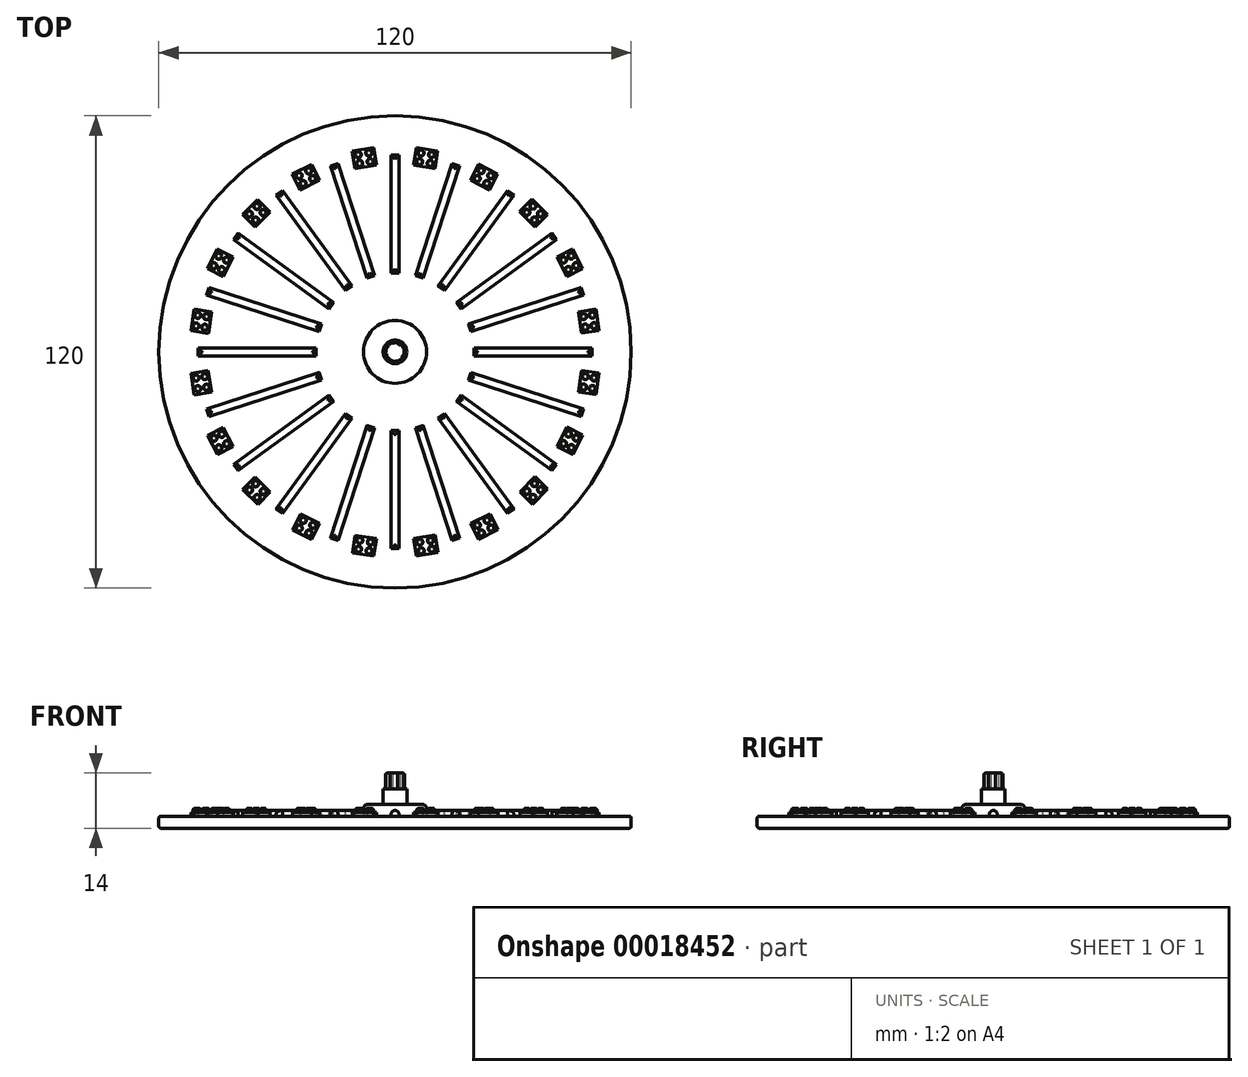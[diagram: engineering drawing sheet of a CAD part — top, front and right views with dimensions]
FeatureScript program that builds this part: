
annotation { "Feature Type Name" : "Feature", "Feature Type Description" : "" }
export const myFeature = defineFeature(function(context is Context, id is Id, definition is map)
    precondition{}
    {
        {
            var Q0;
            Q0=qCreatedBy(makeId("Top.planeOp"),FACE);
            var sketch = newSketch(context, id + "F0", { "sketchPlane" : qUnion([Q0])});
            skCircle(sketch, "E0", {"center": v(0, 0) * mm, "radius": 60 * mm});
            skSolve(sketch);
        }
        {
            var Q0;
            Q0=makeQuery(id+"F0.imprint","IMPRINT",FACE,{"disambiguationData":[TD([[makeQuery(id+"F0.imprint","IMPRINT",EDGE,{"derivedFrom":sQuery(id+"F0.wireOp",EDGE,"E0")}),1.0]])]});
            extrude(context, id + "F1", {"entities" : qUnion([Q0]), "depth" : 3 * mm});
        }
        {
            var Q0;
            Q0=makeQuery(id+"F1.opExtrude","CAP_EDGE",EDGE,{"disambiguationData":[OSD([sQuery(id+"F0.wireOp",EDGE,"E0")])],"isStart":false});
            var Q1;
            Q1=makeQuery(id+"F1.opExtrude","CAP_EDGE",EDGE,{"disambiguationData":[OSD([sQuery(id+"F0.wireOp",EDGE,"E0")])],"isStart":true});
            fillet(context, id + "F2", {"entities" : qUnion([Q0, Q1]), "radius" : 0.5 * mm, "tangentPropagation" : true, "allowEdgeOverflow" : false});
        }
        {
            var Q0;
            Q0=makeQuery(id+"F1.opExtrude","CAP_FACE",FACE,{"disambiguationData":[OSD([sQuery(id+"F0.wireOp",EDGE,"E0")])],"isStart":false});
            var sketch = newSketch(context, id + "F3", { "sketchPlane" : qUnion([Q0])});
            skLineSegment(sketch, "E1", {"start": v(0, 0) * mm, "end": v(0, 59.5) * mm, "construction": true});
            skCircle(sketch, "E2", {"center": v(0, 0) * mm, "radius": 20 * mm, "construction": true});
            skCircle(sketch, "E3", {"center": v(0, 0) * mm, "radius": 50 * mm, "construction": true});
            skCircle(sketch, "E4", {"center": v(0, 0) * mm, "radius": 35 * mm, "construction": true});
            skLineSegment(sketch, "E5.rect.bottom", {"start": v(1, 49.99) * mm, "end": v(-1, 49.99) * mm});
            skLineSegment(sketch, "E5.rect.top", {"start": v(1, 20.01) * mm, "end": v(-1, 20.01) * mm});
            skLineSegment(sketch, "E5.rect.left", {"start": v(1, 49.99) * mm, "end": v(1, 20.01) * mm});
            skLineSegment(sketch, "E5.rect.right", {"start": v(-1, 49.99) * mm, "end": v(-1, 20.01) * mm});
            skPoint(sketch, "E5.rect.middle", {"position": v(0, 35) * mm});
            skCircle(sketch, "E6", {"center": v(0, 0) * mm, "radius": 8 * mm});
            skCircle(sketch, "E7", {"center": v(0, 0) * mm, "radius": 45 * mm, "construction": true});
            skSolve(sketch);
        }
        {
            var Q0;
            Q0=makeQuery(id+"F3.imprint","IMPRINT",FACE,{"disambiguationData":[TD([[makeQuery(id+"F3.imprint","IMPRINT",EDGE,{"derivedFrom":sQuery(id+"F3.wireOp",EDGE,"E5.rect.bottom")}),1.0]])]});
            extrude(context, id + "F4", {"entities" : qUnion([Q0]), "depth" : 1.5 * mm});
        }
        {
            var Q0;
            Q0=makeQuery(id+"F4.opExtrude","CAP_EDGE",EDGE,{"disambiguationData":[OSD([sQuery(id+"F3.wireOp",EDGE,"E5.rect.left")])],"isStart":false});
            var Q1;
            Q1=makeQuery(id+"F4.opExtrude","CAP_EDGE",EDGE,{"disambiguationData":[OSD([sQuery(id+"F3.wireOp",EDGE,"E5.rect.right")])],"isStart":false});
            var Q2;
            Q2=makeQuery(id+"F4.opExtrude","CAP_EDGE",EDGE,{"disambiguationData":[OSD([sQuery(id+"F3.wireOp",EDGE,"E5.rect.top")])],"isStart":false});
            var Q3;
            Q3=makeQuery(id+"F4.opExtrude","CAP_EDGE",EDGE,{"disambiguationData":[OSD([sQuery(id+"F3.wireOp",EDGE,"E5.rect.bottom")])],"isStart":false});
            fillet(context, id + "F5", {"entities" : qUnion([Q0, Q1, Q2, Q3]), "radius" : 1 * mm, "tangentPropagation" : true, "allowEdgeOverflow" : false});
        }
        {
            var Q0;
            Q0=makeQuery(id+"F4.opExtrude","SWEPT_BODY",BODY,{"disambiguationData":[OSD([sQuery(id+"F3.wireOp",EDGE,"E5.rect.bottom"),sQuery(id+"F3.wireOp",EDGE,"E5.rect.top"),sQuery(id+"F3.wireOp",EDGE,"E5.rect.left"),sQuery(id+"F3.wireOp",EDGE,"E5.rect.right")])]});
            var Q1;
            {var subQ0=sQuery(id+"F0.wireOp",EDGE,"E0");Q1=makeQuery(id+"F2.opFillet","BLEND_EDGE",EDGE,{"blendedFrom":[makeQuery(id+"F1.opExtrude","CAP_EDGE",EDGE,{"disambiguationData":[OSD([subQ0])],"isStart":false}),makeQuery(id+"F1.opExtrude","SWEPT_FACE",FACE,{"disambiguationData":[OSD([subQ0])]})],"blendedInto":[makeQuery(id+"F1.opExtrude","SWEPT_FACE",FACE,{"disambiguationData":[OSD([subQ0])]})]});}
            circularPattern(context, id + "F6", {"operationType" : NewBodyOperationType.ADD, "entities" : qUnion([Q0]), "axis" : qUnion([Q1]), "angle" : 18 * degree, "instanceCount" : round(23)});
        }
        {
            var Q0;
            Q0=makeQuery(id+"F3.imprint","IMPRINT",FACE,{"disambiguationData":[TD([[makeQuery(id+"F3.imprint","IMPRINT",EDGE,{"derivedFrom":sQuery(id+"F3.wireOp",EDGE,"E6")}),1.0]])]});
            extrude(context, id + "F7", {"entities" : qUnion([Q0]), "operationType" : NewBodyOperationType.ADD, "depth" : 3 * mm});
        }
        {
            var Q0;
            Q0=makeQuery(id+"F7.opExtrude","CAP_EDGE",EDGE,{"disambiguationData":[OSD([sQuery(id+"F3.wireOp",EDGE,"E6")])],"isStart":false});
            fillet(context, id + "F8", {"entities" : qUnion([Q0]), "radius" : 1 * mm, "tangentPropagation" : true, "allowEdgeOverflow" : false});
        }
        {
            var Q0;
            Q0=makeQuery(id+"F7.opExtrude","CAP_FACE",FACE,{"disambiguationData":[OSD([sQuery(id+"F3.wireOp",EDGE,"E6")])],"isStart":false});
            var sketch = newSketch(context, id + "F9", { "sketchPlane" : qUnion([Q0])});
            skCircle(sketch, "E8", {"center": v(0, 0) * mm, "radius": 3 * mm});
            skSolve(sketch);
        }
        {
            var Q0;
            Q0=makeQuery(id+"F9.imprint","IMPRINT",FACE,{"disambiguationData":[TD([[makeQuery(id+"F9.imprint","IMPRINT",EDGE,{"derivedFrom":sQuery(id+"F9.wireOp",EDGE,"E8")}),1.0]])]});
            extrude(context, id + "F10", {"entities" : qUnion([Q0]), "operationType" : NewBodyOperationType.ADD, "depth" : 4 * mm});
        }
        {
            var Q0;
            Q0=makeQuery(id+"F10.opExtrude","CAP_FACE",FACE,{"disambiguationData":[OSD([sQuery(id+"F9.wireOp",EDGE,"E8")])],"isStart":false});
            var sketch = newSketch(context, id + "F11", { "sketchPlane" : qUnion([Q0])});
            skCircle(sketch, "E9.cCircle", {"center": v(0, 0) * mm, "radius": 2.5 * mm, "construction": true});
            skLineSegment(sketch, "E9.0", {"start": v(2.13, -1.3) * mm, "end": v(0.59, -2.43) * mm});
            skLineSegment(sketch, "E9.1", {"start": v(0.59, -2.43) * mm, "end": v(-1.3, -2.13) * mm});
            skLineSegment(sketch, "E9.2", {"start": v(-1.3, -2.13) * mm, "end": v(-2.43, -0.59) * mm});
            skLineSegment(sketch, "E9.3", {"start": v(-2.43, -0.59) * mm, "end": v(-2.13, 1.3) * mm});
            skLineSegment(sketch, "E9.4", {"start": v(-2.13, 1.3) * mm, "end": v(-0.59, 2.43) * mm});
            skLineSegment(sketch, "E9.5", {"start": v(-0.59, 2.43) * mm, "end": v(1.3, 2.13) * mm});
            skLineSegment(sketch, "E9.6", {"start": v(1.3, 2.13) * mm, "end": v(2.43, 0.59) * mm});
            skLineSegment(sketch, "E9.7", {"start": v(2.43, 0.59) * mm, "end": v(2.13, -1.3) * mm});
            skSolve(sketch);
        }
        {
            var Q0;
            Q0=makeQuery(id+"F11.imprint","IMPRINT",FACE,{"disambiguationData":[TD([[makeQuery(id+"F11.imprint","IMPRINT",EDGE,{"derivedFrom":sQuery(id+"F11.wireOp",EDGE,"E9.0")}),-1.0]])]});
            extrude(context, id + "F12", {"entities" : qUnion([Q0]), "operationType" : NewBodyOperationType.ADD, "depth" : 4 * mm});
        }
        {
            var Q0;
            Q0=makeQuery(id+"F12.opExtrude","CAP_EDGE",EDGE,{"disambiguationData":[OSD([sQuery(id+"F11.wireOp",EDGE,"E9.3")])],"isStart":false});
            var Q1;
            Q1=makeQuery(id+"F12.opExtrude","CAP_EDGE",EDGE,{"disambiguationData":[OSD([sQuery(id+"F11.wireOp",EDGE,"E9.2")])],"isStart":false});
            var Q2;
            Q2=makeQuery(id+"F12.opExtrude","CAP_EDGE",EDGE,{"disambiguationData":[OSD([sQuery(id+"F11.wireOp",EDGE,"E9.1")])],"isStart":false});
            var Q3;
            Q3=makeQuery(id+"F12.opExtrude","CAP_EDGE",EDGE,{"disambiguationData":[OSD([sQuery(id+"F11.wireOp",EDGE,"E9.4")])],"isStart":false});
            var Q4;
            Q4=makeQuery(id+"F12.opExtrude","CAP_EDGE",EDGE,{"disambiguationData":[OSD([sQuery(id+"F11.wireOp",EDGE,"E9.5")])],"isStart":false});
            var Q5;
            Q5=makeQuery(id+"F12.opExtrude","CAP_EDGE",EDGE,{"disambiguationData":[OSD([sQuery(id+"F11.wireOp",EDGE,"E9.6")])],"isStart":false});
            var Q6;
            Q6=makeQuery(id+"F12.opExtrude","CAP_EDGE",EDGE,{"disambiguationData":[OSD([sQuery(id+"F11.wireOp",EDGE,"E9.7")])],"isStart":false});
            var Q7;
            Q7=makeQuery(id+"F12.opExtrude","CAP_EDGE",EDGE,{"disambiguationData":[OSD([sQuery(id+"F11.wireOp",EDGE,"E9.0")])],"isStart":false});
            fillet(context, id + "F13", {"entities" : qUnion([Q0, Q1, Q2, Q3, Q4, Q5, Q6, Q7]), "radius" : 0.5 * mm, "allowEdgeOverflow" : false});
        }
        {
            var Q0;
            Q0=makeQuery(id+"F3.imprint","IMPRINT",FACE,{"disambiguationData":[TD([[makeQuery(id+"F3.imprint","IMPRINT",EDGE,{"derivedFrom":sQuery(id+"F3.wireOp",EDGE,"E5.rect.bottom")}),-1.0]])]});
            var sketch = newSketch(context, id + "F14", { "sketchPlane" : qUnion([Q0])});
            skLineSegment(sketch, "E10", {"start": v(0, 0) * mm, "end": v(9.16, 58.76) * mm, "construction": true});
            skLineSegment(sketch, "E11", {"start": v(0, 0) * mm, "end": v(18.06, 56.37) * mm, "construction": true});
            skLineSegment(sketch, "E12", {"start": v(0, 0) * mm, "end": v(0, 59.7) * mm, "construction": true});
            skLineSegment(sketch, "E13", {"start": v(0, 59.7) * mm, "end": v(9.16, 58.76) * mm, "construction": true});
            skLineSegment(sketch, "E14", {"start": v(9.16, 58.76) * mm, "end": v(0, 59.7) * mm, "construction": true});
            skLineSegment(sketch, "E15", {"start": v(9.16, 58.76) * mm, "end": v(18.06, 56.37) * mm, "construction": true});
            skLineSegment(sketch, "E16", {"start": v(7.33, 47.02) * mm, "end": v(4.7, 47.43) * mm});
            skLineSegment(sketch, "E17", {"start": v(7.33, 47.02) * mm, "end": v(10.14, 46.58) * mm});
            skLineSegment(sketch, "E18", {"start": v(10.14, 46.58) * mm, "end": v(10.83, 51.03) * mm});
            skLineSegment(sketch, "E19", {"start": v(10.83, 51.03) * mm, "end": v(5.4, 51.87) * mm});
            skLineSegment(sketch, "E20", {"start": v(5.4, 51.87) * mm, "end": v(4.7, 47.43) * mm});
            skLineSegment(sketch, "E21.0.MirrorCS", {"start": v(21.36, 42.52) * mm, "end": v(18.81, 43.8) * mm});
            skLineSegment(sketch, "E22.0.MirrorCS", {"start": v(25.75, 45.35) * mm, "end": v(23.73, 41.33) * mm});
            skLineSegment(sketch, "E23.0.MirrorCS", {"start": v(18.81, 43.8) * mm, "end": v(20.83, 47.82) * mm});
            skLineSegment(sketch, "E24.0.MirrorCS", {"start": v(20.83, 47.82) * mm, "end": v(25.75, 45.35) * mm});
            skLineSegment(sketch, "E25.0.MirrorCS", {"start": v(21.36, 42.52) * mm, "end": v(23.73, 41.33) * mm});
            skLineSegment(sketch, "E26", {"start": v(0, 0) * mm, "end": v(-18.56, 57.25) * mm, "construction": true});
            skLineSegment(sketch, "E27", {"start": v(0, 0) * mm, "end": v(-34.89, 48) * mm, "construction": true});
            skLineSegment(sketch, "E28.0.MirrorCS", {"start": v(-33.62, 33.68) * mm, "end": v(-31.74, 35.55) * mm});
            skLineSegment(sketch, "E29.0.MirrorCS", {"start": v(-33.62, 33.68) * mm, "end": v(-35.63, 31.67) * mm});
            skLineSegment(sketch, "E30.0.MirrorCS", {"start": v(-35.63, 31.67) * mm, "end": v(-38.81, 34.85) * mm});
            skLineSegment(sketch, "E31.0.MirrorCS", {"start": v(-38.81, 34.85) * mm, "end": v(-34.92, 38.74) * mm});
            skLineSegment(sketch, "E32.0.MirrorCS", {"start": v(-34.92, 38.74) * mm, "end": v(-31.74, 35.55) * mm});
            skLineSegment(sketch, "E33", {"start": v(0, 0) * mm, "end": v(-48.36, 35.52) * mm, "construction": true});
            skLineSegment(sketch, "E34", {"start": v(0, 0) * mm, "end": v(-58.04, 18.6) * mm, "construction": true});
            skLineSegment(sketch, "E35", {"start": v(0, 0) * mm, "end": v(61.65, 0) * mm, "construction": true});
            skLineSegment(sketch, "E36", {"start": v(61.65, 0) * mm, "end": v(-61.86, 0) * mm, "construction": true});
            skLineSegment(sketch, "E37", {"start": v(0, 0) * mm, "end": v(34.29, 46.69) * mm, "construction": true});
            skLineSegment(sketch, "E38", {"start": v(0, 0) * mm, "end": v(48.15, 35) * mm, "construction": true});
            skLineSegment(sketch, "E39", {"start": v(0, 0) * mm, "end": v(57.22, 18.4) * mm, "construction": true});
            skLineSegment(sketch, "E40.0.MirrorCS", {"start": v(-40.88, 24.52) * mm, "end": v(-44.87, 26.6) * mm});
            skLineSegment(sketch, "E41.0.MirrorCS", {"start": v(-47.41, 21.72) * mm, "end": v(-43.42, 19.64) * mm});
            skLineSegment(sketch, "E42.0.MirrorCS", {"start": v(-44.87, 26.6) * mm, "end": v(-47.41, 21.72) * mm});
            skLineSegment(sketch, "E43.0.MirrorCS", {"start": v(-42.2, 22) * mm, "end": v(-40.88, 24.52) * mm});
            skLineSegment(sketch, "E44.0.MirrorCS", {"start": v(-42.2, 22) * mm, "end": v(-43.42, 19.64) * mm});
            skLineSegment(sketch, "E45.0.MirrorCS", {"start": v(-51.2, 9.88) * mm, "end": v(-46.75, 9.25) * mm});
            skLineSegment(sketch, "E46.0.MirrorCS", {"start": v(-47.52, 3.8) * mm, "end": v(-51.97, 4.43) * mm});
            skLineSegment(sketch, "E47.0.MirrorCS", {"start": v(-51.97, 4.43) * mm, "end": v(-51.2, 9.88) * mm});
            skLineSegment(sketch, "E48.0.MirrorCS", {"start": v(-47.12, 6.62) * mm, "end": v(-47.52, 3.8) * mm});
            skLineSegment(sketch, "E49.0.MirrorCS", {"start": v(-47.12, 6.62) * mm, "end": v(-46.75, 9.25) * mm});
            skLineSegment(sketch, "E50.0.MirrorCS", {"start": v(39.4, 34.2) * mm, "end": v(35.57, 38.14) * mm});
            skLineSegment(sketch, "E51.0.MirrorCS", {"start": v(36.16, 31.06) * mm, "end": v(39.4, 34.2) * mm});
            skLineSegment(sketch, "E52.0.MirrorCS", {"start": v(35.57, 38.14) * mm, "end": v(32.33, 35.01) * mm});
            skLineSegment(sketch, "E53.0.MirrorCS", {"start": v(34.18, 33.1) * mm, "end": v(32.33, 35.01) * mm});
            skLineSegment(sketch, "E54.0.MirrorCS", {"start": v(34.18, 33.1) * mm, "end": v(36.16, 31.06) * mm});
            skLineSegment(sketch, "E55.0.MirrorCS", {"start": v(42.04, 22.3) * mm, "end": v(40.7, 24.8) * mm});
            skLineSegment(sketch, "E56.0.MirrorCS", {"start": v(47.26, 22.05) * mm, "end": v(43.29, 19.95) * mm});
            skLineSegment(sketch, "E57.0.MirrorCS", {"start": v(44.68, 26.91) * mm, "end": v(47.26, 22.05) * mm});
            skLineSegment(sketch, "E58.0.MirrorCS", {"start": v(40.7, 24.8) * mm, "end": v(44.68, 26.91) * mm});
            skLineSegment(sketch, "E59.0.MirrorCS", {"start": v(42.04, 22.3) * mm, "end": v(43.29, 19.95) * mm});
            skLineSegment(sketch, "E60.0.MirrorCS", {"start": v(47.15, 6.4) * mm, "end": v(46.8, 9.02) * mm});
            skLineSegment(sketch, "E61.0.MirrorCS", {"start": v(51.26, 9.63) * mm, "end": v(46.8, 9.02) * mm});
            skLineSegment(sketch, "E62.0.MirrorCS", {"start": v(52, 4.18) * mm, "end": v(51.26, 9.63) * mm});
            skLineSegment(sketch, "E63.0.MirrorCS", {"start": v(47.54, 3.57) * mm, "end": v(52, 4.18) * mm});
            skLineSegment(sketch, "E64.0.MirrorCS", {"start": v(47.15, 6.4) * mm, "end": v(47.54, 3.57) * mm});
            skLineSegment(sketch, "E65.0.MirrorCS", {"start": v(-47.52, -3.8) * mm, "end": v(-51.97, -4.43) * mm});
            skLineSegment(sketch, "E66.0.MirrorCS", {"start": v(-51.97, -4.43) * mm, "end": v(-51.2, -9.88) * mm});
            skLineSegment(sketch, "E67.0.MirrorCS", {"start": v(-47.12, -6.62) * mm, "end": v(-46.75, -9.25) * mm});
            skLineSegment(sketch, "E68.0.MirrorCS", {"start": v(-47.12, -6.62) * mm, "end": v(-47.52, -3.8) * mm});
            skLineSegment(sketch, "E69.0.MirrorCS", {"start": v(-51.2, -9.88) * mm, "end": v(-46.75, -9.25) * mm});
            skLineSegment(sketch, "E70.0.MirrorCS", {"start": v(-47.41, -21.72) * mm, "end": v(-43.42, -19.64) * mm});
            skLineSegment(sketch, "E71.0.MirrorCS", {"start": v(-44.87, -26.6) * mm, "end": v(-47.41, -21.72) * mm});
            skLineSegment(sketch, "E72.0.MirrorCS", {"start": v(-42.2, -22) * mm, "end": v(-43.42, -19.64) * mm});
            skLineSegment(sketch, "E73.0.MirrorCS", {"start": v(-42.2, -22) * mm, "end": v(-40.88, -24.52) * mm});
            skLineSegment(sketch, "E74.0.MirrorCS", {"start": v(-40.88, -24.52) * mm, "end": v(-44.87, -26.6) * mm});
            skLineSegment(sketch, "E75.0.MirrorCS", {"start": v(-35.63, -31.67) * mm, "end": v(-38.81, -34.85) * mm});
            skLineSegment(sketch, "E76.0.MirrorCS", {"start": v(-38.81, -34.85) * mm, "end": v(-34.92, -38.74) * mm});
            skLineSegment(sketch, "E77.0.MirrorCS", {"start": v(-34.92, -38.74) * mm, "end": v(-31.74, -35.55) * mm});
            skLineSegment(sketch, "E78.0.MirrorCS", {"start": v(-33.62, -33.68) * mm, "end": v(-31.74, -35.55) * mm});
            skLineSegment(sketch, "E79.0.MirrorCS", {"start": v(-33.62, -33.68) * mm, "end": v(-35.63, -31.67) * mm});
            skLineSegment(sketch, "E80.0.MirrorCS", {"start": v(-21.65, -42.37) * mm, "end": v(-24.02, -41.17) * mm});
            skLineSegment(sketch, "E81.0.MirrorCS", {"start": v(-21.65, -42.37) * mm, "end": v(-19.12, -43.67) * mm});
            skLineSegment(sketch, "E82.0.MirrorCS", {"start": v(-19.12, -43.67) * mm, "end": v(-21.17, -47.68) * mm});
            skLineSegment(sketch, "E83.0.MirrorCS", {"start": v(-21.17, -47.68) * mm, "end": v(-26.07, -45.17) * mm});
            skLineSegment(sketch, "E84.0.MirrorCS", {"start": v(-26.07, -45.17) * mm, "end": v(-24.02, -41.17) * mm});
            skLineSegment(sketch, "E85.0.MirrorCS", {"start": v(-7.33, -47.02) * mm, "end": v(-10.14, -46.58) * mm});
            skLineSegment(sketch, "E86.0.MirrorCS", {"start": v(-7.33, -47.02) * mm, "end": v(-4.7, -47.43) * mm});
            skLineSegment(sketch, "E87.0.MirrorCS", {"start": v(-5.4, -51.87) * mm, "end": v(-4.7, -47.43) * mm});
            skLineSegment(sketch, "E88.0.MirrorCS", {"start": v(-10.14, -46.58) * mm, "end": v(-10.83, -51.03) * mm});
            skLineSegment(sketch, "E89.0.MirrorCS", {"start": v(-10.83, -51.03) * mm, "end": v(-5.4, -51.87) * mm});
            skLineSegment(sketch, "E90.0.MirrorCS", {"start": v(5.4, -51.87) * mm, "end": v(4.7, -47.43) * mm});
            skLineSegment(sketch, "E91.0.MirrorCS", {"start": v(7.33, -47.02) * mm, "end": v(4.7, -47.43) * mm});
            skLineSegment(sketch, "E92.0.MirrorCS", {"start": v(7.33, -47.02) * mm, "end": v(10.14, -46.58) * mm});
            skLineSegment(sketch, "E93.0.MirrorCS", {"start": v(10.14, -46.58) * mm, "end": v(10.83, -51.03) * mm});
            skLineSegment(sketch, "E94.0.MirrorCS", {"start": v(10.83, -51.03) * mm, "end": v(5.4, -51.87) * mm});
            skLineSegment(sketch, "E95.0.MirrorCS", {"start": v(18.81, -43.8) * mm, "end": v(20.83, -47.82) * mm});
            skLineSegment(sketch, "E96.0.MirrorCS", {"start": v(20.83, -47.82) * mm, "end": v(25.75, -45.35) * mm});
            skLineSegment(sketch, "E97.0.MirrorCS", {"start": v(25.75, -45.35) * mm, "end": v(23.73, -41.33) * mm});
            skLineSegment(sketch, "E98.0.MirrorCS", {"start": v(21.36, -42.52) * mm, "end": v(18.81, -43.8) * mm});
            skLineSegment(sketch, "E99.0.MirrorCS", {"start": v(21.36, -42.52) * mm, "end": v(23.73, -41.33) * mm});
            skLineSegment(sketch, "E100.0.MirrorCS", {"start": v(35.57, -38.14) * mm, "end": v(32.33, -35.01) * mm});
            skLineSegment(sketch, "E101.0.MirrorCS", {"start": v(39.4, -34.2) * mm, "end": v(35.57, -38.14) * mm});
            skLineSegment(sketch, "E102.0.MirrorCS", {"start": v(36.16, -31.06) * mm, "end": v(39.4, -34.2) * mm});
            skLineSegment(sketch, "E103.0.MirrorCS", {"start": v(34.18, -33.1) * mm, "end": v(32.33, -35.01) * mm});
            skLineSegment(sketch, "E104.0.MirrorCS", {"start": v(34.18, -33.1) * mm, "end": v(36.16, -31.06) * mm});
            skLineSegment(sketch, "E105.0.MirrorCS", {"start": v(44.68, -26.91) * mm, "end": v(47.26, -22.05) * mm});
            skLineSegment(sketch, "E106.0.MirrorCS", {"start": v(40.7, -24.8) * mm, "end": v(44.68, -26.91) * mm});
            skLineSegment(sketch, "E107.0.MirrorCS", {"start": v(42.04, -22.3) * mm, "end": v(40.7, -24.8) * mm});
            skLineSegment(sketch, "E108.0.MirrorCS", {"start": v(42.04, -22.3) * mm, "end": v(43.29, -19.95) * mm});
            skLineSegment(sketch, "E109.0.MirrorCS", {"start": v(47.26, -22.05) * mm, "end": v(43.29, -19.95) * mm});
            skLineSegment(sketch, "E110.0.MirrorCS", {"start": v(51.26, -9.63) * mm, "end": v(46.8, -9.02) * mm});
            skLineSegment(sketch, "E111.0.MirrorCS", {"start": v(47.15, -6.4) * mm, "end": v(47.54, -3.57) * mm});
            skLineSegment(sketch, "E112.0.MirrorCS", {"start": v(47.15, -6.4) * mm, "end": v(46.8, -9.02) * mm});
            skLineSegment(sketch, "E113.0.MirrorCS", {"start": v(47.54, -3.57) * mm, "end": v(52, -4.18) * mm});
            skLineSegment(sketch, "E114.0.MirrorCS", {"start": v(52, -4.18) * mm, "end": v(51.26, -9.63) * mm});
            skSolve(sketch);
        }
        {
            var Q0;
            Q0=makeQuery(id+"F14.imprint","IMPRINT",FACE,{"disambiguationData":[TD([[makeQuery(id+"F14.imprint","IMPRINT",EDGE,{"derivedFrom":sQuery(id+"F14.wireOp",EDGE,"E16")}),-1.0]])]});
            extrude(context, id + "F15", {"entities" : qUnion([Q0]), "depth" : 1 * mm});
        }
        {
            var Q0;
            Q0=makeQuery(id+"F15.opExtrude","CAP_FACE",FACE,{"disambiguationData":[OSD([sQuery(id+"F14.wireOp",EDGE,"E16"),sQuery(id+"F14.wireOp",EDGE,"E17"),sQuery(id+"F14.wireOp",EDGE,"E18"),sQuery(id+"F14.wireOp",EDGE,"E19"),sQuery(id+"F14.wireOp",EDGE,"E20")])],"isStart":false});
            var sketch = newSketch(context, id + "F16", { "sketchPlane" : qUnion([Q0])});
            skLineSegment(sketch, "E115", {"start": v(8.12, 51.45) * mm, "end": v(7.42, 47) * mm, "construction": true});
            skLineSegment(sketch, "E116", {"start": v(7.42, 47) * mm, "end": v(7.77, 49.23) * mm, "construction": true});
            skLineSegment(sketch, "E117", {"start": v(7.77, 49.23) * mm, "end": v(5.05, 49.65) * mm, "construction": true});
            skLineSegment(sketch, "E118", {"start": v(7.77, 49.23) * mm, "end": v(10.49, 48.8) * mm, "construction": true});
            skLineSegment(sketch, "E119", {"start": v(9.13, 49.01) * mm, "end": v(9.48, 51.24) * mm, "construction": true});
            skLineSegment(sketch, "E120", {"start": v(6.41, 49.44) * mm, "end": v(6.76, 51.66) * mm, "construction": true});
            skLineSegment(sketch, "E121", {"start": v(6.41, 49.44) * mm, "end": v(6.07, 47.21) * mm, "construction": true});
            skLineSegment(sketch, "E122", {"start": v(9.13, 49.01) * mm, "end": v(8.78, 46.8) * mm});
            skLineSegment(sketch, "E123", {"start": v(6.24, 48.33) * mm, "end": v(4.88, 48.54) * mm, "construction": true});
            skLineSegment(sketch, "E124", {"start": v(6.24, 48.33) * mm, "end": v(10.31, 47.7) * mm, "construction": true});
            skLineSegment(sketch, "E125", {"start": v(9.3, 50.13) * mm, "end": v(10.66, 49.91) * mm, "construction": true});
            skLineSegment(sketch, "E126", {"start": v(9.3, 50.13) * mm, "end": v(5.23, 50.76) * mm, "construction": true});
            skPoint(sketch, "E127", {"position": v(8.96, 47.9) * mm});
            skPoint(sketch, "E128", {"position": v(6.59, 50.55) * mm});
            skCircle(sketch, "E129", {"center": v(6.59, 50.55) * mm, "radius": 0.5 * mm});
            skCircle(sketch, "E130", {"center": v(9.3, 50.13) * mm, "radius": 0.5 * mm});
            skCircle(sketch, "E131", {"center": v(6.24, 48.33) * mm, "radius": 0.5 * mm});
            skCircle(sketch, "E132", {"center": v(8.96, 47.9) * mm, "radius": 0.5 * mm});
            skSolve(sketch);
        }
        {
            var Q0;
            Q0=makeQuery(id+"F16.imprint","IMPRINT",FACE,{"disambiguationData":[TD([[makeQuery(id+"F16.imprint","IMPRINT",EDGE,{"derivedFrom":sQuery(id+"F16.wireOp",EDGE,"E129")}),1.0]])]});
            var Q1;
            Q1=makeQuery(id+"F16.imprint","IMPRINT",FACE,{"disambiguationData":[TD([[makeQuery(id+"F16.imprint","IMPRINT",EDGE,{"derivedFrom":sQuery(id+"F16.wireOp",EDGE,"E130")}),1.0]])]});
            var Q2;
            Q2=makeQuery(id+"F16.imprint","IMPRINT",FACE,{"disambiguationData":[TD([[makeQuery(id+"F16.imprint","IMPRINT",EDGE,{"derivedFrom":sQuery(id+"F16.wireOp",EDGE,"E131")}),1.0]])]});
            var Q3;
            {var subQ0=sQuery(id+"F16.wireOp",EDGE,"E132");var subQ1=sQuery(id+"F16.wireOp",EDGE,"E122");var subQ3=makeQuery(id+"F16.imprint","INTERSECT",VERTEX,{"disambiguationData":[OD(0.0)],"derivedFrom":[subQ1,subQ0]});Q3=makeQuery(id+"F16.imprint","IMPRINT",FACE,{"disambiguationData":[TD([[makeQuery(id+"F16.imprint","IMPRINT",EDGE,{"disambiguationData":[TD([[subQ3,1.0]])],"derivedFrom":subQ1}),1.0]])]});}
            var Q4;
            {var subQ0=sQuery(id+"F16.wireOp",EDGE,"E132");var subQ1=sQuery(id+"F16.wireOp",EDGE,"E122");var subQ3=makeQuery(id+"F16.imprint","INTERSECT",VERTEX,{"disambiguationData":[OD(0.0)],"derivedFrom":[subQ1,subQ0]});Q4=makeQuery(id+"F16.imprint","IMPRINT",FACE,{"disambiguationData":[TD([[makeQuery(id+"F16.imprint","IMPRINT",EDGE,{"disambiguationData":[TD([[subQ3,1.0]])],"derivedFrom":subQ1}),-1.0]])]});}
            extrude(context, id + "F17", {"entities" : qUnion([Q0, Q1, Q2, Q3, Q4]), "depth" : 1 * mm});
        }
        {
            var Q0;
            Q0=makeQuery(id+"F17.opExtrude","CAP_FACE",FACE,{"disambiguationData":[OSD([sQuery(id+"F16.wireOp",EDGE,"E131")])],"isStart":false});
            var sketch = newSketch(context, id + "F18", { "sketchPlane" : qUnion([Q0])});
            skPoint(sketch, "E133", {"position": v(6.24, 48.33) * mm});
            skCircle(sketch, "E134", {"center": v(6.59, 50.55) * mm, "radius": 0.8 * mm});
            skCircle(sketch, "E135", {"center": v(9.3, 50.13) * mm, "radius": 0.8 * mm});
            skCircle(sketch, "E136", {"center": v(6.24, 48.33) * mm, "radius": 0.8 * mm});
            skCircle(sketch, "E137", {"center": v(8.96, 47.9) * mm, "radius": 0.8 * mm});
            skSolve(sketch);
        }
        {
            var Q0;
            Q0=makeQuery(id+"F18.imprint","IMPRINT",FACE,{"disambiguationData":[TD([[makeQuery(id+"F18.imprint","IMPRINT",EDGE,{"derivedFrom":sQuery(id+"F18.wireOp",EDGE,"E135")}),1.0]])]});
            var Q1;
            Q1=makeQuery(id+"F18.imprint","IMPRINT",FACE,{"disambiguationData":[TD([[makeQuery(id+"F18.imprint","IMPRINT",EDGE,{"derivedFrom":sQuery(id+"F18.wireOp",EDGE,"E137")}),1.0]])]});
            var Q2;
            Q2=makeQuery(id+"F18.imprint","IMPRINT",FACE,{"disambiguationData":[TD([[makeQuery(id+"F18.imprint","IMPRINT",EDGE,{"derivedFrom":sQuery(id+"F18.wireOp",EDGE,"E134")}),1.0]])]});
            var Q3;
            Q3=makeQuery(id+"F18.imprint","IMPRINT",FACE,{"disambiguationData":[TD([[makeQuery(id+"F18.imprint","IMPRINT",EDGE,{"derivedFrom":sQuery(id+"F18.wireOp",EDGE,"E136")}),1.0]])]});
            var Q4;
            Q4=makeQuery(id+"F18.imprint","IMPRINT",FACE,{"disambiguationData":[TD([[makeQuery(id+"F18.imprint","IMPRINT",EDGE,{"derivedFrom":makeQuery(id+"F17.opExtrude","CAP_EDGE",EDGE,{"disambiguationData":[OSD([sQuery(id+"F16.wireOp",EDGE,"E131")])],"isStart":false})}),1.0]])]});
            extrude(context, id + "F19", {"entities" : qUnion([Q0, Q1, Q2, Q3, Q4]), "operationType" : NewBodyOperationType.ADD, "oppositeDirection" : true, "depth" : .5 * mm});
        }
        {
            var Q0;
            Q0=makeQuery(id+"F19.opExtrude","CAP_EDGE",EDGE,{"disambiguationData":[OSD([sQuery(id+"F18.wireOp",EDGE,"E137")])],"isStart":true});
            var Q1;
            Q1=makeQuery(id+"F19.opExtrude","CAP_EDGE",EDGE,{"disambiguationData":[OSD([sQuery(id+"F18.wireOp",EDGE,"E136")])],"isStart":true});
            var Q2;
            Q2=makeQuery(id+"F19.boolean.opBoolean","MERGE",FACE,{"derivedFrom":[makeQuery(id+"F17.opExtrude","CAP_FACE",FACE,{"disambiguationData":[OSD([sQuery(id+"F16.wireOp",EDGE,"E129")])],"isStart":false}),makeQuery(id+"F19.opExtrude","CAP_FACE",FACE,{"disambiguationData":[OSD([sQuery(id+"F18.wireOp",EDGE,"E134")])],"isStart":true})]});
            var Q3;
            Q3=makeQuery(id+"F19.opExtrude","CAP_EDGE",EDGE,{"disambiguationData":[OSD([sQuery(id+"F18.wireOp",EDGE,"E135")])],"isStart":true});
            fillet(context, id + "F20", {"entities" : qUnion([Q0, Q1, Q2, Q3]), "radius" : 0.5 * mm, "tangentPropagation" : true, "allowEdgeOverflow" : false});
        }
        {
            var Q0;
            Q0=makeQuery(id+"F15.opExtrude","SWEPT_BODY",BODY,{"disambiguationData":[OSD([sQuery(id+"F14.wireOp",EDGE,"E16"),sQuery(id+"F14.wireOp",EDGE,"E17"),sQuery(id+"F14.wireOp",EDGE,"E18"),sQuery(id+"F14.wireOp",EDGE,"E19"),sQuery(id+"F14.wireOp",EDGE,"E20")])]});
            var Q1;
            Q1=makeQuery(id+"F19.opExtrude","SWEPT_BODY",BODY,{"disambiguationData":[OSD([sQuery(id+"F18.wireOp",EDGE,"E136")])]});
            var Q2;
            Q2=makeQuery(id+"F19.opExtrude","SWEPT_BODY",BODY,{"disambiguationData":[OSD([sQuery(id+"F18.wireOp",EDGE,"E134")])]});
            var Q3;
            Q3=makeQuery(id+"F19.opExtrude","SWEPT_BODY",BODY,{"disambiguationData":[OSD([sQuery(id+"F18.wireOp",EDGE,"E135")])]});
            var Q4;
            Q4=makeQuery(id+"F19.opExtrude","SWEPT_BODY",BODY,{"disambiguationData":[OSD([sQuery(id+"F18.wireOp",EDGE,"E137")])]});
            var Q5;
            Q5=makeQuery(id+"F17.opExtrude","SWEPT_BODY",BODY,{"disambiguationData":[OSD([sQuery(id+"F16.wireOp",EDGE,"E131")])]});
            var Q6;
            Q6=makeQuery(id+"F17.opExtrude","SWEPT_BODY",BODY,{"disambiguationData":[OSD([sQuery(id+"F16.wireOp",EDGE,"E132")])]});
            var Q7;
            Q7=makeQuery(id+"F17.opExtrude","SWEPT_BODY",BODY,{"disambiguationData":[OSD([sQuery(id+"F16.wireOp",EDGE,"E130")])]});
            var Q8;
            Q8=makeQuery(id+"F17.opExtrude","SWEPT_BODY",BODY,{"disambiguationData":[OSD([sQuery(id+"F16.wireOp",EDGE,"E129")])]});
            var Q9;
            Q9=sQuery(id+"F9.wireOp",EDGE,"E8");
            circularPattern(context, id + "F21", {"entities" : qUnion([Q0, Q1, Q2, Q3, Q4, Q5, Q6, Q7, Q8]), "axis" : qUnion([Q9]), "angle" : 18 * degree, "instanceCount" : round(20)});
        }
    });
